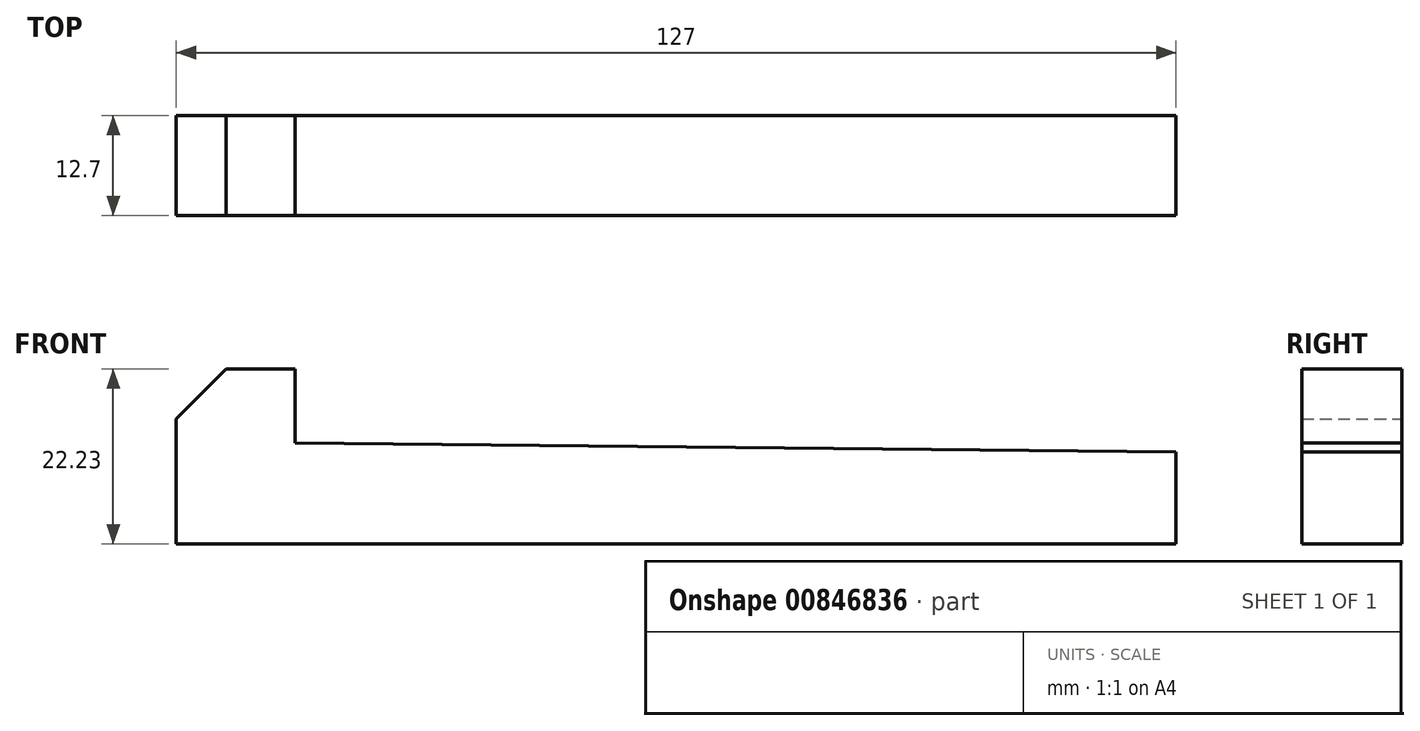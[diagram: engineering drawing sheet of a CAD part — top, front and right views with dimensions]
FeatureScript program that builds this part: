
annotation { "Feature Type Name" : "Feature", "Feature Type Description" : "" }
export const myFeature = defineFeature(function(context is Context, id is Id, definition is map)
    precondition{}
    {
        {
            var Q0;
            Q0=qCreatedBy(makeId("Front.planeOp"),FACE);
            var sketch = newSketch(context, id + "F0", { "sketchPlane" : qUnion([Q0])});
            skLineSegment(sketch, "E0", {"start": v(99.22, 0) * mm, "end": v(-27.78, 0) * mm});
            skLineSegment(sketch, "E1", {"start": v(-27.78, 0) * mm, "end": v(-27.78, 15.87) * mm});
            skLineSegment(sketch, "E2", {"start": v(-27.78, 15.87) * mm, "end": v(-21.43, 22.22) * mm});
            skLineSegment(sketch, "E3", {"start": v(-21.43, 22.22) * mm, "end": v(-12.7, 22.23) * mm});
            skLineSegment(sketch, "E4", {"start": v(-12.7, 22.22) * mm, "end": v(-12.7, 12.83) * mm});
            skLineSegment(sketch, "E5", {"start": v(-12.7, 12.83) * mm, "end": v(99.22, 11.67) * mm});
            skLineSegment(sketch, "E6", {"start": v(99.22, 11.67) * mm, "end": v(99.22, 0) * mm});
            skLineSegment(sketch, "E7", {"start": v(0, 12.7) * mm, "end": v(0, 0) * mm, "construction": true});
            skSolve(sketch);
        }
        {
            var Q0;
            Q0 = qSketchRegion(id + "F0", true);
            extrude(context, id + "F1", {"entities" : qUnion([Q0]), "depth" : 12.7 * mm, "offsetDistance" : 25.4 * mm, "symmetric" : true});
        }
        {
            var Q0;
            Q0=qCreatedBy(makeId("Right.planeOp"), FACE);
            var sketch = newSketch(context, id + "F2", { "sketchPlane" : qUnion([Q0])});
            skLineSegment(sketch, "E8.0", {"start": v(0, 12.7) * mm, "end": v(0, 0) * mm});
            skCircle(sketch, "E9", {"center": v(0, 12.7) * mm, "radius": 0.98 * mm});
            skSolve(sketch);
        }
    });
